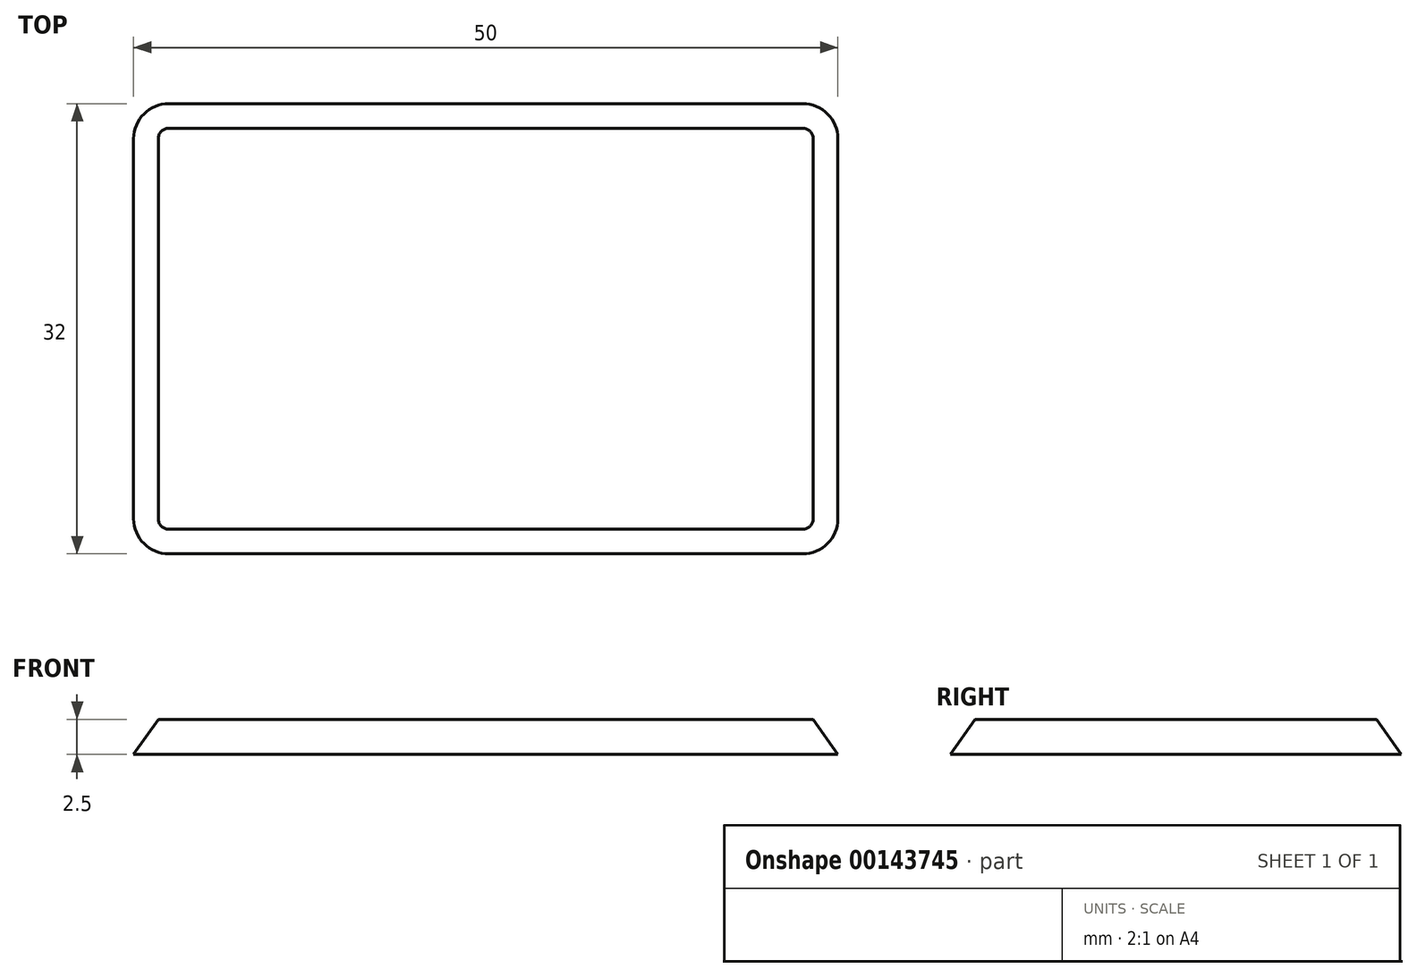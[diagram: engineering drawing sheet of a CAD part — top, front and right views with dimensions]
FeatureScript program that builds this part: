
annotation { "Feature Type Name" : "Feature", "Feature Type Description" : "" }
export const myFeature = defineFeature(function(context is Context, id is Id, definition is map)
    precondition{}
    {
        {
            var Q0;
            Q0=qCreatedBy(makeId("Top.planeOp"),FACE);
            var sketch = newSketch(context, id + "F0", { "sketchPlane" : qUnion([Q0])});
            skLineSegment(sketch, "E0.bottom", {"start": v(25, 16) * mm, "end": v(-25, 16) * mm});
            skLineSegment(sketch, "E0.top", {"start": v(25, -16) * mm, "end": v(-25, -16) * mm});
            skLineSegment(sketch, "E0.left", {"start": v(25, 16) * mm, "end": v(25, -16) * mm});
            skLineSegment(sketch, "E0.right", {"start": v(-25, 16) * mm, "end": v(-25, -16) * mm});
            skPoint(sketch, "E0.middle", {"position": v(0, 0) * mm});
            skSolve(sketch);
        }
        {
            var Q0;
            Q0=makeQuery(id+"F0.imprint","IMPRINT",FACE,{"disambiguationData":[TD([[makeQuery(id+"F0.imprint","IMPRINT",EDGE,{"derivedFrom":sQuery(id+"F0.wireOp",EDGE,"E0.bottom")}),1.0]])]});
            extrude(context, id + "F1", {"entities" : qUnion([Q0]), "offsetDistance" : 25 * mm, "depth" : 2.5 * mm});
        }
        {
            var Q0;
            Q0=makeQuery(id+"F1.opExtrude","SWEPT_EDGE",EDGE,{"disambiguationData":[OSD([sQuery(id+"F0.wireOp",EDGE,"E0.top"),sQuery(id+"F0.wireOp",EDGE,"E0.right")])]});
            var Q1;
            Q1=makeQuery(id+"F1.opExtrude","SWEPT_EDGE",EDGE,{"disambiguationData":[OSD([sQuery(id+"F0.wireOp",EDGE,"E0.top"),sQuery(id+"F0.wireOp",EDGE,"E0.left")])]});
            var Q2;
            Q2=makeQuery(id+"F1.opExtrude","SWEPT_EDGE",EDGE,{"disambiguationData":[OSD([sQuery(id+"F0.wireOp",EDGE,"E0.bottom"),sQuery(id+"F0.wireOp",EDGE,"E0.left")])]});
            var Q3;
            Q3=makeQuery(id+"F1.opExtrude","SWEPT_EDGE",EDGE,{"disambiguationData":[OSD([sQuery(id+"F0.wireOp",EDGE,"E0.bottom"),sQuery(id+"F0.wireOp",EDGE,"E0.right")])]});
            fillet(context, id + "F2", {"entities" : qUnion([Q0, Q1, Q2, Q3]), "radius" : 2.5 * mm, "tangentPropagation" : true, "allowEdgeOverflow" : false});
        }
        {
            var Q0;
            Q0=makeQuery(id+"F1.opExtrude","CAP_EDGE",EDGE,{"disambiguationData":[OSD([sQuery(id+"F0.wireOp",EDGE,"E0.top")])],"isStart":false});
            var Q1;
            {var subQ0=sQuery(id+"F0.wireOp",EDGE,"E0.right");var subQ1=sQuery(id+"F0.wireOp",EDGE,"E0.top");Q1=makeQuery(id+"F2.opFillet","BLEND_EDGE",EDGE,{"blendedFrom":[makeQuery(id+"F1.opExtrude","SWEPT_EDGE",EDGE,{"disambiguationData":[OSD([subQ1,subQ0])]}),makeQuery(id+"F1.opExtrude","CAP_FACE",FACE,{"disambiguationData":[OSD([sQuery(id+"F0.wireOp",EDGE,"E0.bottom"),subQ1,sQuery(id+"F0.wireOp",EDGE,"E0.left"),subQ0])],"isStart":false})],"blendedInto":[makeQuery(id+"F1.opExtrude","CAP_FACE",FACE,{"disambiguationData":[OSD([sQuery(id+"F0.wireOp",EDGE,"E0.bottom"),subQ1,sQuery(id+"F0.wireOp",EDGE,"E0.left"),subQ0])],"isStart":false})]});}
            var Q2;
            Q2=makeQuery(id+"F1.opExtrude","CAP_EDGE",EDGE,{"disambiguationData":[OSD([sQuery(id+"F0.wireOp",EDGE,"E0.right")])],"isStart":false});
            var Q3;
            {var subQ0=sQuery(id+"F0.wireOp",EDGE,"E0.right");var subQ1=sQuery(id+"F0.wireOp",EDGE,"E0.bottom");Q3=makeQuery(id+"F2.opFillet","BLEND_EDGE",EDGE,{"blendedFrom":[makeQuery(id+"F1.opExtrude","SWEPT_EDGE",EDGE,{"disambiguationData":[OSD([subQ1,subQ0])]}),makeQuery(id+"F1.opExtrude","CAP_FACE",FACE,{"disambiguationData":[OSD([subQ1,sQuery(id+"F0.wireOp",EDGE,"E0.top"),sQuery(id+"F0.wireOp",EDGE,"E0.left"),subQ0])],"isStart":false})],"blendedInto":[makeQuery(id+"F1.opExtrude","CAP_FACE",FACE,{"disambiguationData":[OSD([subQ1,sQuery(id+"F0.wireOp",EDGE,"E0.top"),sQuery(id+"F0.wireOp",EDGE,"E0.left"),subQ0])],"isStart":false})]});}
            var Q4;
            Q4=makeQuery(id+"F1.opExtrude","CAP_EDGE",EDGE,{"disambiguationData":[OSD([sQuery(id+"F0.wireOp",EDGE,"E0.bottom")])],"isStart":false});
            var Q5;
            {var subQ0=sQuery(id+"F0.wireOp",EDGE,"E0.left");var subQ1=sQuery(id+"F0.wireOp",EDGE,"E0.bottom");Q5=makeQuery(id+"F2.opFillet","BLEND_EDGE",EDGE,{"blendedFrom":[makeQuery(id+"F1.opExtrude","SWEPT_EDGE",EDGE,{"disambiguationData":[OSD([subQ1,subQ0])]}),makeQuery(id+"F1.opExtrude","CAP_FACE",FACE,{"disambiguationData":[OSD([subQ1,sQuery(id+"F0.wireOp",EDGE,"E0.top"),subQ0,sQuery(id+"F0.wireOp",EDGE,"E0.right")])],"isStart":false})],"blendedInto":[makeQuery(id+"F1.opExtrude","CAP_FACE",FACE,{"disambiguationData":[OSD([subQ1,sQuery(id+"F0.wireOp",EDGE,"E0.top"),subQ0,sQuery(id+"F0.wireOp",EDGE,"E0.right")])],"isStart":false})]});}
            var Q6;
            Q6=makeQuery(id+"F1.opExtrude","CAP_EDGE",EDGE,{"disambiguationData":[OSD([sQuery(id+"F0.wireOp",EDGE,"E0.left")])],"isStart":false});
            var Q7;
            {var subQ0=sQuery(id+"F0.wireOp",EDGE,"E0.left");var subQ1=sQuery(id+"F0.wireOp",EDGE,"E0.top");Q7=makeQuery(id+"F2.opFillet","BLEND_EDGE",EDGE,{"blendedFrom":[makeQuery(id+"F1.opExtrude","SWEPT_EDGE",EDGE,{"disambiguationData":[OSD([subQ1,subQ0])]}),makeQuery(id+"F1.opExtrude","CAP_FACE",FACE,{"disambiguationData":[OSD([sQuery(id+"F0.wireOp",EDGE,"E0.bottom"),subQ1,subQ0,sQuery(id+"F0.wireOp",EDGE,"E0.right")])],"isStart":false})],"blendedInto":[makeQuery(id+"F1.opExtrude","CAP_FACE",FACE,{"disambiguationData":[OSD([sQuery(id+"F0.wireOp",EDGE,"E0.bottom"),subQ1,subQ0,sQuery(id+"F0.wireOp",EDGE,"E0.right")])],"isStart":false})]});}
            chamfer(context, id + "F3", {"entities" : qUnion([Q0, Q1, Q2, Q3, Q4, Q5, Q6, Q7]), "chamferType" : ChamferType.OFFSET_ANGLE, "width" : 2.5 * mm, "oppositeDirection" : false, "angle" : 35 * degree, "tangentPropagation" : true});
        }
    });
